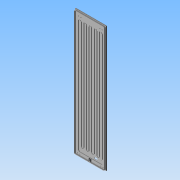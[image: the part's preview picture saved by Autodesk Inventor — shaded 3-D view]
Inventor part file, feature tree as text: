
AUTODESK INVENTOR PART (.ipt)
format: ipt  version: 2013 (Build 170138000, 138)  size: 342,528 bytes
history: native  units: in
note: dims shown in document units (in); Inventor stores cm internally (conversion verified against a paired STEP export)
features: other x14, extrude x4, hole x1, plane x1
ambient origin geometry x8: Origin, YZ Plane, XZ Plane, XY Plane, X Axis, Y Axis, Z Axis, Center Point
bodies: Solid1 (feature_tree)
feature tree (20):
  other  "CHICKA Ply back"
  other  "Blocks"
  extrude  "Stock Extrusion"  Depth=23.8125in
  extrude  "Main rope pocket"  Depth=96.0in
  other  "Side profile reference"
  hole  "Hole1"  [1 undecoded]
  plane  "Work Plane1"
  extrude  "Through Panel Extrusion5"  Depth=86.0in
  extrude  "Outline Channel"  Depth=1.0in
  other  "Stock"
  other  "LEDPocket"
  other  "TwoLineColumn"
  other  "TwoLineColumnEnd"
  other  "15mm Neon profile"
  other  "U Bolt hole and bore"
  other  "U-Bolt holes"
  other  "WeatherProof panel"
  other  "Border"
  other  "15mm Neon profile:1"
  other  "15mm Neon profile:2"
note: 1 required parameter value undecoded (feature->parameter linkage not recoverable at this tier; creation-order binding heuristic only, values carry confidence <= 0.55)
